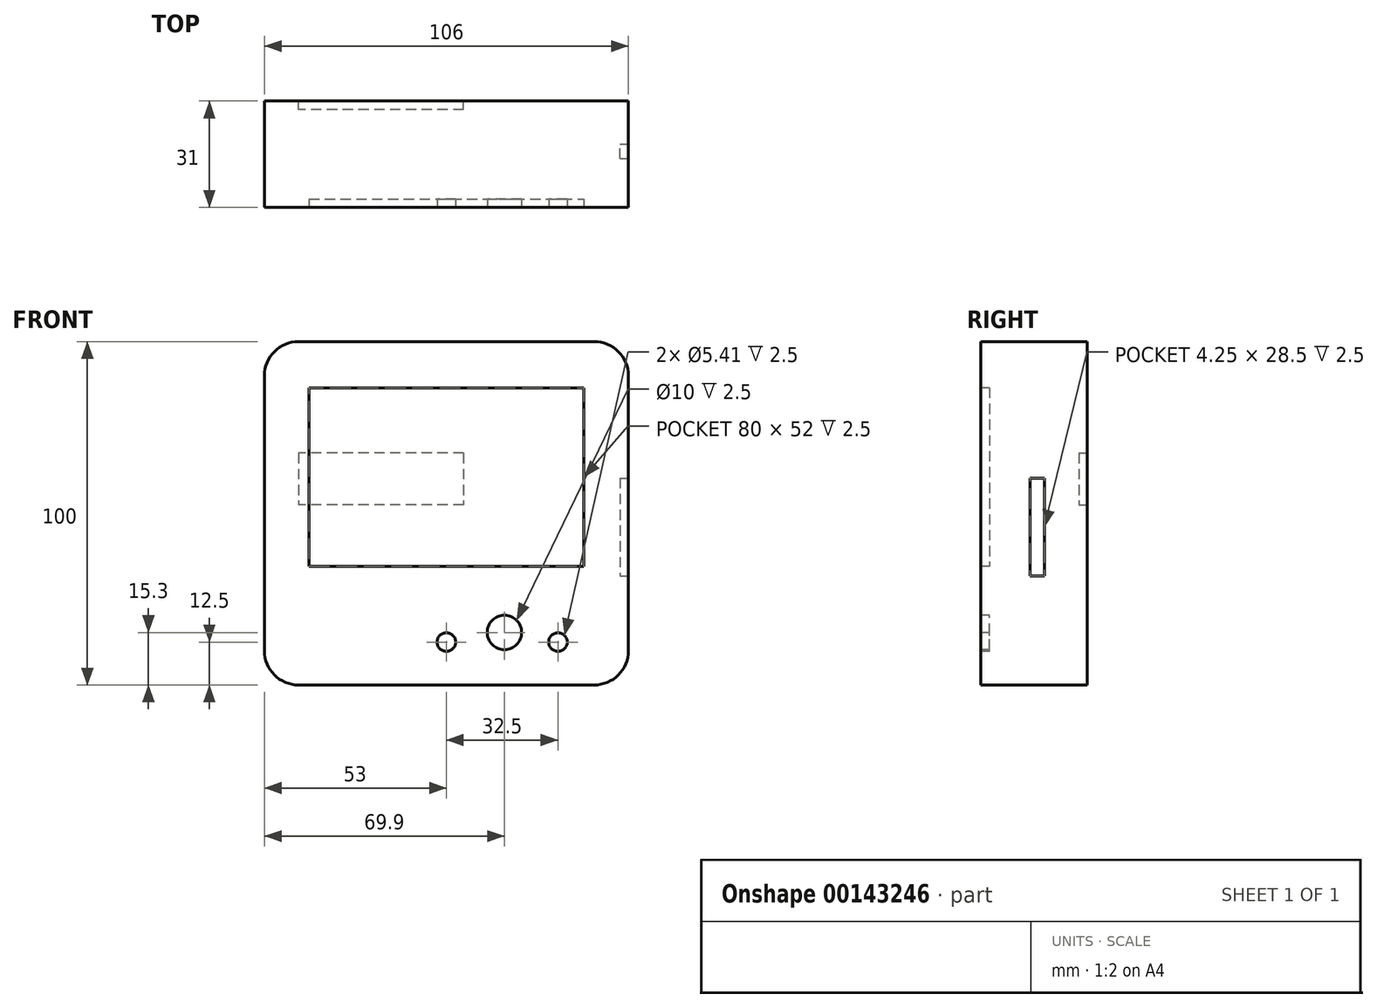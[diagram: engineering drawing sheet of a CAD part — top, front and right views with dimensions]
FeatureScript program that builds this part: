
annotation { "Feature Type Name" : "Feature", "Feature Type Description" : "" }
export const myFeature = defineFeature(function(context is Context, id is Id, definition is map)
    precondition{}
    {
        {
            var Q0;
            Q0=qCreatedBy(makeId("Front.planeOp"),FACE);
            var sketch = newSketch(context, id + "F0", { "sketchPlane" : qUnion([Q0])});
            skLineSegment(sketch, "E0.bottom", {"start": v(53, -50) * mm, "end": v(-53, -50) * mm});
            skLineSegment(sketch, "E0.top", {"start": v(53, 50) * mm, "end": v(-53, 50) * mm});
            skLineSegment(sketch, "E0.left", {"start": v(53, -50) * mm, "end": v(53, 50) * mm});
            skLineSegment(sketch, "E0.right", {"start": v(-53, -50) * mm, "end": v(-53, 50) * mm});
            skPoint(sketch, "E0.middle", {"position": v(0, 0) * mm});
            skLineSegment(sketch, "E1.bottom", {"start": v(-40, 36.5) * mm, "end": v(40, 36.5) * mm});
            skLineSegment(sketch, "E1.top", {"start": v(-40, -15.5) * mm, "end": v(40, -15.5) * mm});
            skLineSegment(sketch, "E1.left", {"start": v(-40, 36.5) * mm, "end": v(-40, -15.5) * mm});
            skLineSegment(sketch, "E1.right", {"start": v(40, 36.5) * mm, "end": v(40, -15.5) * mm});
            skCircle(sketch, "E2", {"center": v(16.9, -34.7) * mm, "radius": 5 * mm});
            skLineSegment(sketch, "E3", {"start": v(-40, 36.5) * mm, "end": v(-53, 36.5) * mm, "construction": true});
            skLineSegment(sketch, "E4", {"start": v(40, 36.5) * mm, "end": v(53, 36.5) * mm, "construction": true});
            skCircle(sketch, "E5", {"center": v(0, -37.5) * mm, "radius": 2.7 * mm});
            skCircle(sketch, "E6", {"center": v(32.5, -37.5) * mm, "radius": 2.7 * mm});
            skLineSegment(sketch, "E7", {"start": v(0, -37.5) * mm, "end": v(32.5, -37.5) * mm, "construction": true});
            skLineSegment(sketch, "E8", {"start": v(16.9, -34.7) * mm, "end": v(16.9, -37.5) * mm, "construction": true});
            skSolve(sketch);
        }
        {
            var Q0;
            Q0=makeQuery(id+"F0.imprint","IMPRINT",FACE,{"disambiguationData":[TD([[makeQuery(id+"F0.imprint","IMPRINT",EDGE,{"derivedFrom":sQuery(id+"F0.wireOp",EDGE,"E0.bottom")}),-1.0]])]});
            var Q1;
            Q1=makeQuery(id+"F0.imprint","IMPRINT",FACE,{"disambiguationData":[TD([[makeQuery(id+"F0.imprint","IMPRINT",EDGE,{"derivedFrom":sQuery(id+"F0.wireOp",EDGE,"E1.bottom")}),-1.0]])]});
            var Q2;
            Q2=makeQuery(id+"F0.imprint","IMPRINT",FACE,{"disambiguationData":[TD([[makeQuery(id+"F0.imprint","IMPRINT",EDGE,{"derivedFrom":sQuery(id+"F0.wireOp",EDGE,"E5")}),1.0]])]});
            var Q3;
            Q3=makeQuery(id+"F0.imprint","IMPRINT",FACE,{"disambiguationData":[TD([[makeQuery(id+"F0.imprint","IMPRINT",EDGE,{"derivedFrom":sQuery(id+"F0.wireOp",EDGE,"E2")}),1.0]])]});
            var Q4;
            Q4=makeQuery(id+"F0.imprint","IMPRINT",FACE,{"disambiguationData":[TD([[makeQuery(id+"F0.imprint","IMPRINT",EDGE,{"derivedFrom":sQuery(id+"F0.wireOp",EDGE,"E6")}),1.0]])]});
            extrude(context, id + "F1", {"entities" : qUnion([Q0, Q1, Q2, Q3, Q4]), "oppositeDirection" : true, "depth" : 31 * mm});
        }
        {
            var Q0;
            Q0=makeQuery(id+"F1.opExtrude","SWEPT_EDGE",EDGE,{"disambiguationData":[OSD([sQuery(id+"F0.wireOp",EDGE,"E0.bottom"),sQuery(id+"F0.wireOp",EDGE,"E0.left")])]});
            var Q1;
            Q1=makeQuery(id+"F1.opExtrude","SWEPT_EDGE",EDGE,{"disambiguationData":[OSD([sQuery(id+"F0.wireOp",EDGE,"E0.top"),sQuery(id+"F0.wireOp",EDGE,"E0.left")])]});
            var Q2;
            Q2=makeQuery(id+"F1.opExtrude","SWEPT_EDGE",EDGE,{"disambiguationData":[OSD([sQuery(id+"F0.wireOp",EDGE,"E0.top"),sQuery(id+"F0.wireOp",EDGE,"E0.right")])]});
            var Q3;
            Q3=makeQuery(id+"F1.opExtrude","SWEPT_EDGE",EDGE,{"disambiguationData":[OSD([sQuery(id+"F0.wireOp",EDGE,"E0.bottom"),sQuery(id+"F0.wireOp",EDGE,"E0.right")])]});
            fillet(context, id + "F2", {"entities" : qUnion([Q0, Q1, Q2, Q3]), "radius" : 10 * mm, "tangentPropagation" : true, "allowEdgeOverflow" : false});
        }
        {
            var Q0;
            Q0=makeQuery(id+"F0.imprint","IMPRINT",FACE,{"disambiguationData":[TD([[makeQuery(id+"F0.imprint","IMPRINT",EDGE,{"derivedFrom":sQuery(id+"F0.wireOp",EDGE,"E1.bottom")}),-1.0]])]});
            var Q1;
            Q1=makeQuery(id+"F0.imprint","IMPRINT",FACE,{"disambiguationData":[TD([[makeQuery(id+"F0.imprint","IMPRINT",EDGE,{"derivedFrom":sQuery(id+"F0.wireOp",EDGE,"E5")}),1.0]])]});
            var Q2;
            Q2=makeQuery(id+"F0.imprint","IMPRINT",FACE,{"disambiguationData":[TD([[makeQuery(id+"F0.imprint","IMPRINT",EDGE,{"derivedFrom":sQuery(id+"F0.wireOp",EDGE,"E2")}),1.0]])]});
            var Q3;
            Q3=makeQuery(id+"F0.imprint","IMPRINT",FACE,{"disambiguationData":[TD([[makeQuery(id+"F0.imprint","IMPRINT",EDGE,{"derivedFrom":sQuery(id+"F0.wireOp",EDGE,"E6")}),1.0]])]});
            extrude(context, id + "F3", {"entities" : qUnion([Q0, Q1, Q2, Q3]), "operationType" : NewBodyOperationType.REMOVE, "oppositeDirection" : true, "depth" : 2.5 * mm});
        }
        {
            var Q0;
            Q0=makeQuery(id+"F1.opExtrude","CAP_FACE",FACE,{"disambiguationData":[OSD([sQuery(id+"F0.wireOp",EDGE,"E0.bottom"),sQuery(id+"F0.wireOp",EDGE,"E0.top"),sQuery(id+"F0.wireOp",EDGE,"E0.left"),sQuery(id+"F0.wireOp",EDGE,"E0.right")])],"isStart":false});
            var sketch = newSketch(context, id + "F4", { "sketchPlane" : qUnion([Q0])});
            skLineSegment(sketch, "E9.bottom", {"start": v(-5, 17.5) * mm, "end": v(43, 17.5) * mm});
            skLineSegment(sketch, "E9.top", {"start": v(-5, 2.5) * mm, "end": v(43, 2.5) * mm});
            skLineSegment(sketch, "E9.left", {"start": v(-5, 17.5) * mm, "end": v(-5, 2.5) * mm});
            skLineSegment(sketch, "E9.right", {"start": v(43, 17.5) * mm, "end": v(43, 2.5) * mm});
            skSolve(sketch);
        }
        {
            var Q0;
            Q0=makeQuery(id+"F4.imprint","IMPRINT",FACE,{"disambiguationData":[TD([[makeQuery(id+"F4.imprint","IMPRINT",EDGE,{"derivedFrom":sQuery(id+"F4.wireOp",EDGE,"E9.bottom")}),-1.0]])]});
            extrude(context, id + "F5", {"entities" : qUnion([Q0]), "operationType" : NewBodyOperationType.REMOVE, "oppositeDirection" : true, "depth" : 2.5 * mm});
        }
        {
            var Q0;
            Q0=makeQuery(id+"F1.opExtrude","SWEPT_FACE",FACE,{"disambiguationData":[OSD([sQuery(id+"F0.wireOp",EDGE,"E0.left")])]});
            var sketch = newSketch(context, id + "F6", { "sketchPlane" : qUnion([Q0])});
            skLineSegment(sketch, "E10.bottom", {"start": v(14.25, 10.25) * mm, "end": v(18.5, 10.25) * mm});
            skLineSegment(sketch, "E10.top", {"start": v(14.25, -18.25) * mm, "end": v(18.5, -18.25) * mm});
            skLineSegment(sketch, "E10.left", {"start": v(14.25, 10.25) * mm, "end": v(14.25, -18.25) * mm});
            skLineSegment(sketch, "E10.right", {"start": v(18.5, 10.25) * mm, "end": v(18.5, -18.25) * mm});
            skSolve(sketch);
        }
        {
            var Q0;
            Q0=makeQuery(id+"F6.imprint","IMPRINT",FACE,{"disambiguationData":[TD([[makeQuery(id+"F6.imprint","IMPRINT",EDGE,{"derivedFrom":sQuery(id+"F6.wireOp",EDGE,"E10.bottom")}),-1.0]])]});
            extrude(context, id + "F7", {"entities" : qUnion([Q0]), "operationType" : NewBodyOperationType.REMOVE, "oppositeDirection" : true, "depth" : 2.5 * mm});
        }
    });
